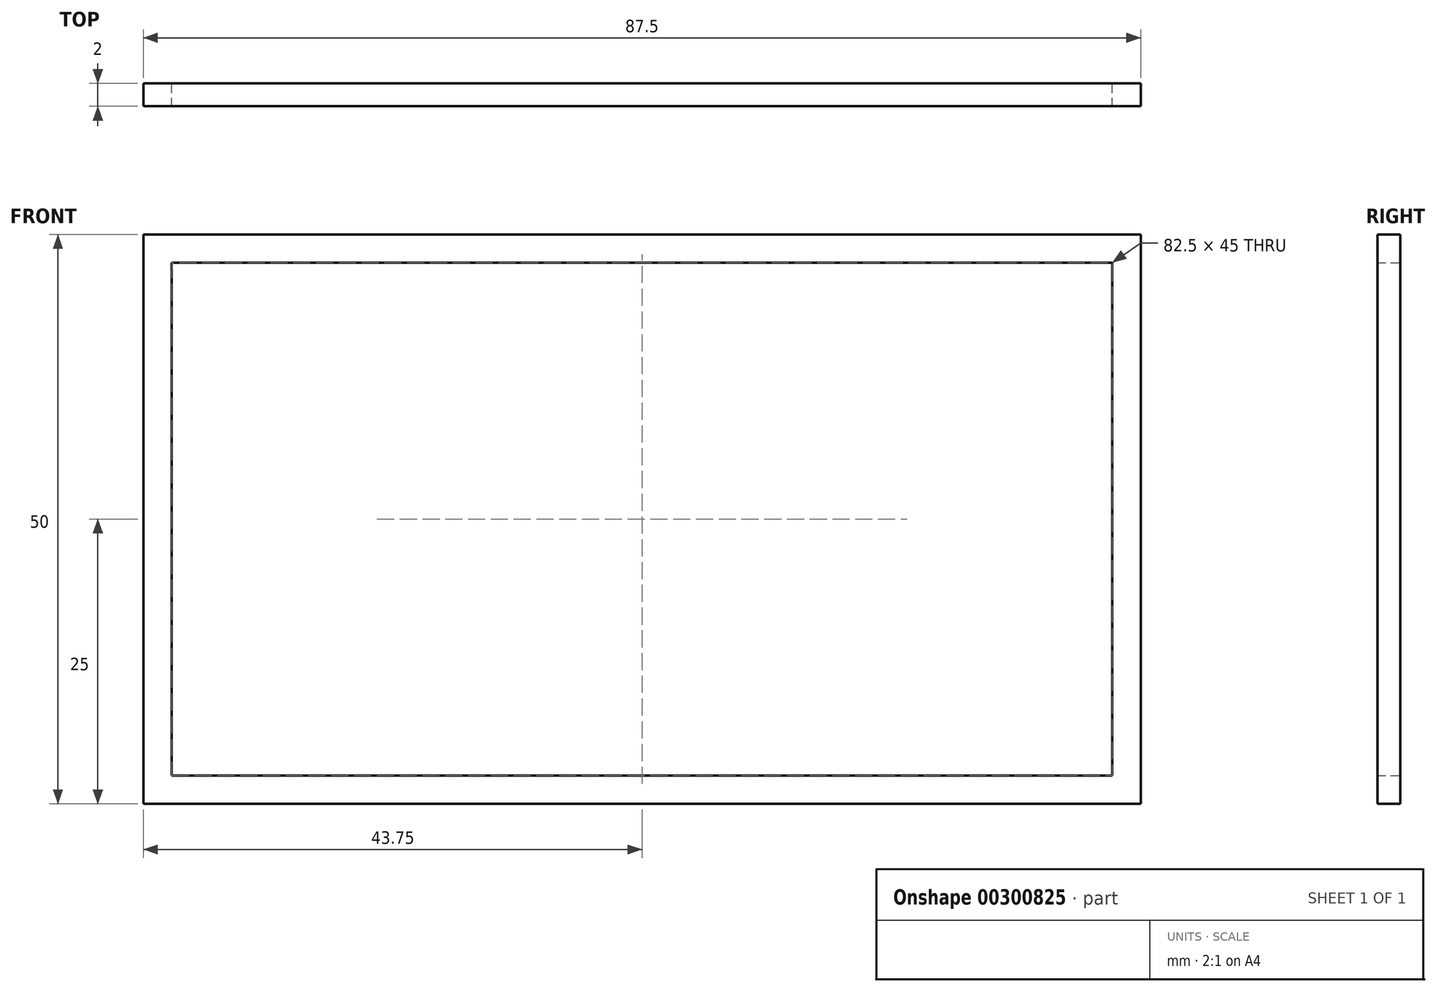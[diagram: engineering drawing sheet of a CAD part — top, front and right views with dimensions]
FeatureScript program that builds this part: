
annotation { "Feature Type Name" : "Feature", "Feature Type Description" : "" }
export const myFeature = defineFeature(function(context is Context, id is Id, definition is map)
    precondition{}
    {
        {
            var Q0;
            Q0=qCreatedBy(makeId("Front.planeOp"),FACE);
            var sketch = newSketch(context, id + "F0", { "sketchPlane" : qUnion([Q0])});
            skLineSegment(sketch, "E0.bottom", {"start": v(0, 0) * mm, "end": v(1750, 0) * mm});
            skLineSegment(sketch, "E0.top", {"start": v(0, -1000) * mm, "end": v(1750, -1000) * mm});
            skLineSegment(sketch, "E0.left", {"start": v(0, 0) * mm, "end": v(0, -1000) * mm});
            skLineSegment(sketch, "E0.right", {"start": v(1750, 0) * mm, "end": v(1750, -1000) * mm});
            skLineSegment(sketch, "E1.bottom", {"start": v(50, -50) * mm, "end": v(1700, -50) * mm});
            skLineSegment(sketch, "E1.top", {"start": v(50, -950) * mm, "end": v(1700, -950) * mm});
            skLineSegment(sketch, "E1.left", {"start": v(50, -50) * mm, "end": v(50, -950) * mm});
            skLineSegment(sketch, "E1.right", {"start": v(1700, -50) * mm, "end": v(1700, -950) * mm});
            skSolve(sketch);
        }
        {
            var Q0;
            Q0=makeQuery(id+"F0.imprint","IMPRINT",FACE,{"disambiguationData":[TD([[makeQuery(id+"F0.imprint","IMPRINT",EDGE,{"derivedFrom":sQuery(id+"F0.wireOp",EDGE,"E0.bottom")}),-1.0]])]});
            extrude(context, id + "F1", {"entities" : qUnion([Q0]), "depth" : 40 * mm});
        }
        {
            var Q0;
            Q0=makeQuery(id+"F1.opExtrude","SWEPT_BODY",BODY,{"disambiguationData":[OSD([sQuery(id+"F0.wireOp",EDGE,"E0.bottom"),sQuery(id+"F0.wireOp",EDGE,"E0.top"),sQuery(id+"F0.wireOp",EDGE,"E0.left"),sQuery(id+"F0.wireOp",EDGE,"E0.right"),sQuery(id+"F0.wireOp",EDGE,"E1.bottom"),sQuery(id+"F0.wireOp",EDGE,"E1.top"),sQuery(id+"F0.wireOp",EDGE,"E1.left"),sQuery(id+"F0.wireOp",EDGE,"E1.right")])]});
            var Q1;
            Q1=qCreatedBy(makeId("Origin.pointOp"),VERTEX);
            var Q2;
            Q2=qCreatedBy(makeId("Origin.pointOp"),VERTEX);
            transform(context, id + "F2", {"entities" : qUnion([Q0]), "transformType" : TransformType.SCALE_UNIFORMLY, "scale" : 0.05, "scalePoint" : qUnion([Q2]), "makeCopy" : false});
        }
    });
